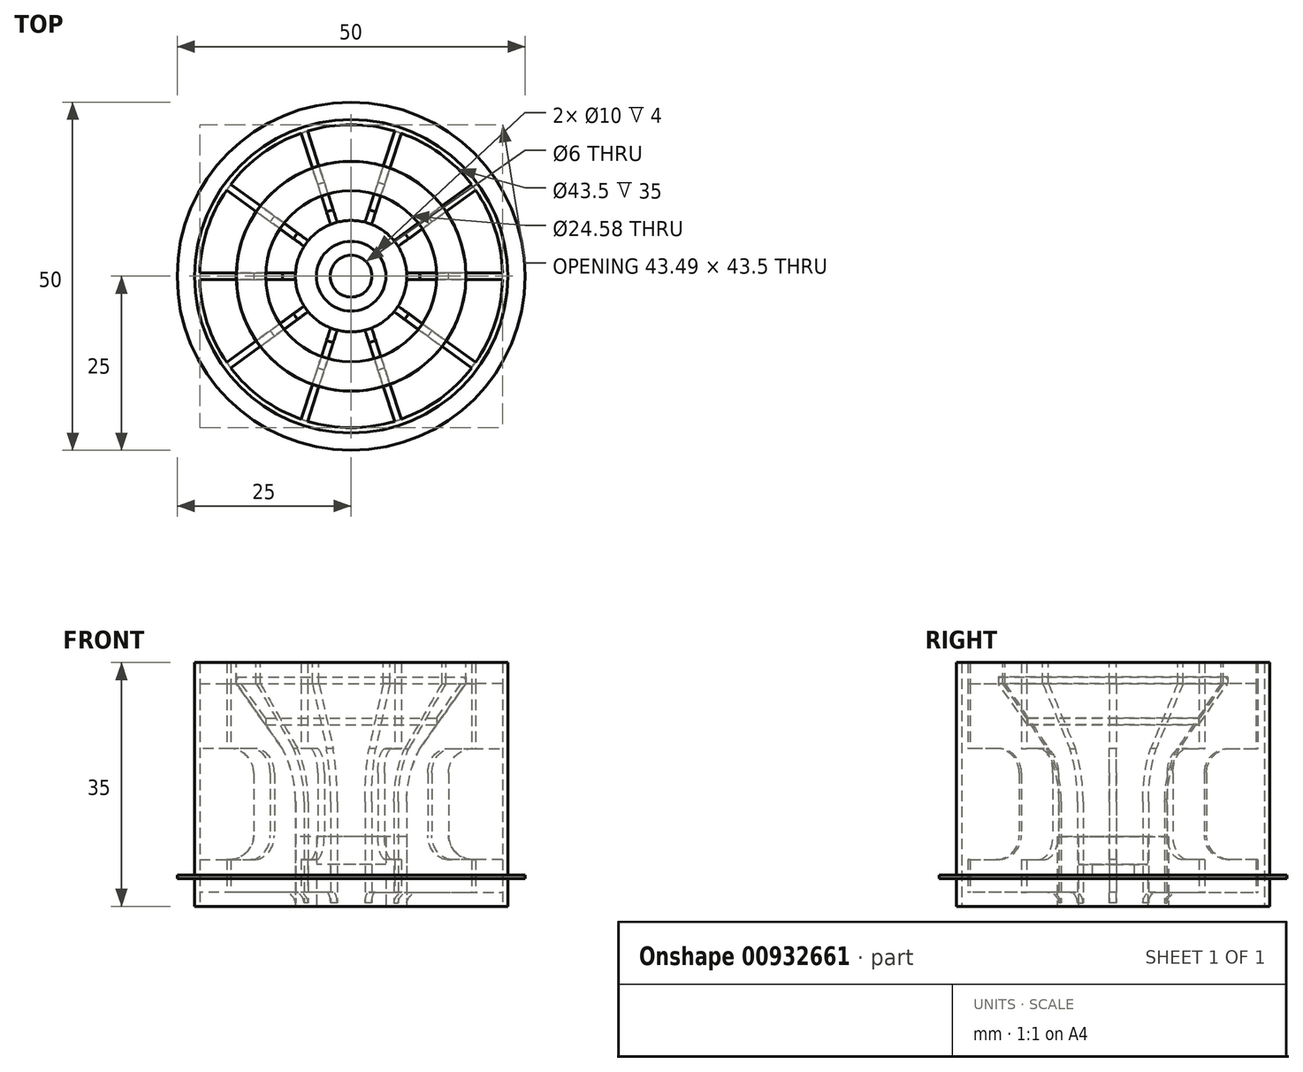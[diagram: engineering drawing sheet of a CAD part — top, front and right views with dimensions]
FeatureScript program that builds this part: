
annotation { "Feature Type Name" : "Feature", "Feature Type Description" : "" }
export const myFeature = defineFeature(function(context is Context, id is Id, definition is map)
    precondition{}
    {
        {
            var Q0;
            Q0=qCreatedBy(makeId("Top.planeOp"),FACE);
            var sketch = newSketch(context, id + "F0", { "sketchPlane" : qUnion([Q0])});
            skCircle(sketch, "E0", {"center": v(0, 0) * mm, "radius": 22.5 * mm});
            skCircle(sketch, "E1", {"center": v(0, 0) * mm, "radius": 21.75 * mm});
            skCircle(sketch, "E2", {"center": v(0, 0) * mm, "radius": 5 * mm});
            skCircle(sketch, "E3", {"center": v(0, 0) * mm, "radius": 8 * mm});
            skSolve(sketch);
        }
        {
            var Q0;
            Q0=makeQuery(id+"F0.imprint","IMPRINT",FACE,{"disambiguationData":[TD([[makeQuery(id+"F0.imprint","IMPRINT",EDGE,{"derivedFrom":sQuery(id+"F0.wireOp",EDGE,"E0")}),1.0]])]});
            extrude(context, id + "F1", {"entities" : qUnion([Q0]), "depth" : 35 * mm, "offsetDistance" : 25 * mm});
        }
        {
            var Q0;
            Q0=makeQuery(id+"F0.imprint","IMPRINT",FACE,{"disambiguationData":[TD([[makeQuery(id+"F0.imprint","IMPRINT",EDGE,{"derivedFrom":sQuery(id+"F0.wireOp",EDGE,"E2")}),-1.0]])]});
            extrude(context, id + "F2", {"entities" : qUnion([Q0]), "depth" : 4 * mm, "offsetDistance" : 25 * mm});
        }
        {
            var Q0;
            Q0=makeQuery(id+"F2.opExtrude","CAP_FACE",FACE,{"disambiguationData":[OSD([sQuery(id+"F0.wireOp",EDGE,"E2"),sQuery(id+"F0.wireOp",EDGE,"E3")])],"isStart":false});
            var sketch = newSketch(context, id + "F3", { "sketchPlane" : qUnion([Q0])});
            skCircle(sketch, "E4", {"center": v(0, 0) * mm, "radius": 3 * mm});
            skCircle(sketch, "E5", {"center": v(0, 0) * mm, "radius": 8 * mm});
            skSolve(sketch);
        }
        {
            var Q0;
            Q0=makeQuery(id+"F3.imprint","IMPRINT",FACE,{"disambiguationData":[TD([[makeQuery(id+"F3.imprint","IMPRINT",EDGE,{"derivedFrom":sQuery(id+"F3.wireOp",EDGE,"E5")}),1.0]])]});
            var Q1;
            Q1=makeQuery(id+"F3.imprint","IMPRINT",FACE,{"disambiguationData":[TD([[makeQuery(id+"F3.imprint","IMPRINT",EDGE,{"derivedFrom":sQuery(id+"F3.wireOp",EDGE,"E4")}),-1.0]])]});
            extrude(context, id + "F4", {"entities" : qUnion([Q0, Q1]), "operationType" : NewBodyOperationType.ADD, "depth" : 2 * mm, "offsetDistance" : 25 * mm});
        }
        {
            var Q0;
            Q0=makeQuery(id+"F4.opExtrude","CAP_FACE",FACE,{"disambiguationData":[OSD([sQuery(id+"F3.wireOp",EDGE,"E4"),sQuery(id+"F3.wireOp",EDGE,"E5")])],"isStart":false});
            var sketch = newSketch(context, id + "F5", { "sketchPlane" : qUnion([Q0])});
            skCircle(sketch, "E6", {"center": v(0, 0) * mm, "radius": 8 * mm});
            skCircle(sketch, "E7", {"center": v(0, 0) * mm, "radius": 5 * mm});
            skSolve(sketch);
        }
        {
            var Q0;
            Q0=makeQuery(id+"F5.imprint","IMPRINT",FACE,{"disambiguationData":[TD([[makeQuery(id+"F5.imprint","IMPRINT",EDGE,{"derivedFrom":sQuery(id+"F5.wireOp",EDGE,"E6")}),1.0]])]});
            extrude(context, id + "F6", {"entities" : qUnion([Q0]), "operationType" : NewBodyOperationType.ADD, "depth" : 4 * mm, "offsetDistance" : 25 * mm});
        }
        {
            var Q0;
            Q0=makeQuery(id+"F1.opExtrude","CAP_FACE",FACE,{"disambiguationData":[OSD([sQuery(id+"F0.wireOp",EDGE,"E0"),sQuery(id+"F0.wireOp",EDGE,"E1")])],"isStart":false});
            var sketch = newSketch(context, id + "F7", { "sketchPlane" : qUnion([Q0])});
            skCircle(sketch, "E8", {"center": v(0, 0) * mm, "radius": 16.5 * mm});
            skCircle(sketch, "E9", {"center": v(0, 0) * mm, "radius": 22.5 * mm});
            skSolve(sketch);
        }
        {
            var Q0;
            Q0=makeQuery(id+"F7.imprint","IMPRINT",FACE,{"disambiguationData":[TD([[makeQuery(id+"F7.imprint","IMPRINT",EDGE,{"derivedFrom":sQuery(id+"F7.wireOp",EDGE,"E8")}),-1.0]])]});
            extrude(context, id + "F8", {"entities" : qUnion([Q0]), "operationType" : NewBodyOperationType.ADD, "oppositeDirection" : true, "depth" : 3 * mm, "offsetDistance" : 25 * mm});
        }
        {
            var Q0;
            Q0=qCreatedBy(makeId("Front.planeOp"),FACE);
            var sketch = newSketch(context, id + "F9", { "sketchPlane" : qUnion([Q0])});
            skLineSegment(sketch, "E10.left", {"start": v(0, 0) * mm, "end": v(0, 6.73) * mm});
            skLineSegment(sketch, "E10.right", {"start": v(-8, 2) * mm, "end": v(-8, 15) * mm});
            skLineSegment(sketch, "E11.top", {"start": v(-16.5, 32) * mm, "end": v(-21, 32) * mm});
            skLineSegment(sketch, "E11.left", {"start": v(0, 0) * mm, "end": v(0, 32) * mm});
            skLineSegment(sketch, "E12", {"start": v(-21, 32) * mm, "end": v(-16.5, 32) * mm});
            skLineSegment(sketch, "E13", {"start": v(-16.5, 32) * mm, "end": v(-9.88, 22.65) * mm});
            skArc(sketch, "E14", {"start": v(-8, 15) * mm, "mid": v(-8.48, 18.94) * mm, "end": v(-9.88, 22.65) * mm});
            skPoint(sketch, "E15.left.end.orphan", {"position": v(-8, 20) * mm});
            skLineSegment(sketch, "E16", {"start": v(-15.83, 32) * mm, "end": v(-12.3, 27) * mm});
            skLineSegment(sketch, "E17", {"start": v(-12.3, 27) * mm, "end": v(-12.3, 26.06) * mm});
            skLineSegment(sketch, "E18", {"start": v(-15.83, 32) * mm, "end": v(-16.5, 32.94) * mm});
            skLineSegment(sketch, "E19", {"start": v(-16.5, 32.94) * mm, "end": v(-16.5, 32) * mm});
            skLineSegment(sketch, "E20.top", {"start": v(-9.71, 2) * mm, "end": v(-21, 2) * mm});
            skPoint(sketch, "E11.bottom.start.orphan", {"position": v(-8, 0) * mm});
            skArc(sketch, "E21", {"start": v(-8, 0) * mm, "mid": v(-8.43, 1.41) * mm, "end": v(-9.79, 2) * mm});
            skPoint(sketch, "E21.second.point", {"position": v(-11.5, 0) * mm});
            skPoint(sketch, "E21.third.point", {"position": v(-9.79, 2) * mm});
            skLineSegment(sketch, "E22.bottom", {"start": v(-21, 6.73) * mm, "end": v(-17.5, 6.73) * mm});
            skLineSegment(sketch, "E22.top", {"start": v(-21, 22.65) * mm, "end": v(-17.7, 22.65) * mm});
            skLineSegment(sketch, "E22.right", {"start": v(-14, 10.23) * mm, "end": v(-14, 19.73) * mm});
            skPoint(sketch, "E23.orphan", {"position": v(-14, 22.65) * mm});
            skLineSegment(sketch, "E24", {"start": v(-17.7, 22.65) * mm, "end": v(-17.5, 22.65) * mm});
            skLineSegment(sketch, "E25.right", {"start": v(-14, 19.73) * mm, "end": v(-14, 19.15) * mm});
            skArc(sketch, "E26", {"start": v(-14, 19.15) * mm, "mid": v(-15.03, 21.62) * mm, "end": v(-17.5, 22.65) * mm});
            skPoint(sketch, "E27.start.orphan", {"position": v(-17.5, 6.73) * mm});
            skArc(sketch, "E28", {"start": v(-17.5, 6.73) * mm, "mid": v(-15.03, 7.75) * mm, "end": v(-14, 10.23) * mm});
            skPoint(sketch, "E29.bottom.start.orphan", {"position": v(-14, 6.73) * mm});
            skLineSegment(sketch, "E30", {"start": v(-8, 2) * mm, "end": v(-8, 0) * mm});
            skLineSegment(sketch, "E31", {"start": v(0, 0) * mm, "end": v(-22.5, 0) * mm});
            skLineSegment(sketch, "E32", {"start": v(-22.5, 0) * mm, "end": v(-22.5, 4) * mm});
            skLineSegment(sketch, "E33.bottom", {"start": v(-22.5, 4) * mm, "end": v(-25, 4) * mm});
            skLineSegment(sketch, "E33.top", {"start": v(-22.5, 4.5) * mm, "end": v(-25, 4.5) * mm});
            skLineSegment(sketch, "E33.left", {"start": v(-22.5, 4) * mm, "end": v(-22.5, 4.5) * mm});
            skLineSegment(sketch, "E33.right", {"start": v(-25, 4) * mm, "end": v(-25, 4.5) * mm});
            skLineSegment(sketch, "E34", {"start": v(-21, 2) * mm, "end": v(-21.75, 2) * mm});
            skLineSegment(sketch, "E35.top", {"start": v(-21, 6.73) * mm, "end": v(-21.75, 6.73) * mm});
            skLineSegment(sketch, "E35.right", {"start": v(-21.75, 2) * mm, "end": v(-21.75, 6.73) * mm});
            skLineSegment(sketch, "E36.bottom", {"start": v(-21, 22.65) * mm, "end": v(-21.75, 22.65) * mm});
            skLineSegment(sketch, "E36.top", {"start": v(-21, 32) * mm, "end": v(-21.75, 32) * mm});
            skLineSegment(sketch, "E36.right", {"start": v(-21.75, 22.65) * mm, "end": v(-21.75, 32) * mm});
            skSolve(sketch);
        }
        {
            var Q0;
            Q0=makeQuery(id+"F9.imprint","IMPRINT",FACE,{"disambiguationData":[TD([[makeQuery(id+"F9.imprint","IMPRINT",EDGE,{"derivedFrom":sQuery(id+"F9.wireOp",EDGE,"E10.right")}),1.0]])]});
            var Q1;
            Q1=sQuery(id+"F9.wireOp",EDGE,"E11.left");
            revolve(context, id + "F10", {"surfaceOperationType" : NewSurfaceOperationType.NEW, "entities" : qUnion([Q0]), "axis" : qUnion([Q1]), "revolveType" : RevolveType.FULL});
        }
        {
            var Q0;
            Q0=makeQuery(id+"F2.opExtrude","CAP_FACE",FACE,{"disambiguationData":[OSD([sQuery(id+"F0.wireOp",EDGE,"E2"),sQuery(id+"F0.wireOp",EDGE,"E3")])],"isStart":true});
            var sketch = newSketch(context, id + "F11", { "sketchPlane" : qUnion([Q0])});
            skCircle(sketch, "E37", {"center": v(0, 0) * mm, "radius": 8 * mm});
            skLineSegment(sketch, "E38", {"start": v(0, 0) * mm, "end": v(-21, 0) * mm});
            skLineSegment(sketch, "E39.bottom", {"start": v(-7.98, -0.5) * mm, "end": v(-21, -0.5) * mm});
            skLineSegment(sketch, "E39.top", {"start": v(-7.98, 0.5) * mm, "end": v(-21, 0.5) * mm});
            skPoint(sketch, "E39.middle", {"position": v(-10.5, 0) * mm});
            skLineSegment(sketch, "E40.1.0", {"start": v(-6.75, -4.29) * mm, "end": v(-17.28, -11.94) * mm});
            skPoint(sketch, "E40.1.1", {"position": v(-8.5, -6.17) * mm});
            skLineSegment(sketch, "E40.1.2", {"start": v(-6.17, -5.1) * mm, "end": v(-16.7, -12.74) * mm});
            skLineSegment(sketch, "E40.2.0", {"start": v(-2.94, -7.44) * mm, "end": v(-6.96, -19.81) * mm});
            skPoint(sketch, "E40.2.1", {"position": v(-3.24, -9.99) * mm});
            skLineSegment(sketch, "E40.2.2", {"start": v(-2, -7.75) * mm, "end": v(-6.01, -20.12) * mm});
            skLineSegment(sketch, "E40.3.0", {"start": v(2, -7.75) * mm, "end": v(6.01, -20.12) * mm});
            skPoint(sketch, "E40.3.1", {"position": v(3.24, -9.99) * mm});
            skLineSegment(sketch, "E40.3.2", {"start": v(2.94, -7.44) * mm, "end": v(6.96, -19.81) * mm});
            skLineSegment(sketch, "E40.4.0", {"start": v(6.17, -5.1) * mm, "end": v(16.7, -12.74) * mm});
            skPoint(sketch, "E40.4.1", {"position": v(8.5, -6.17) * mm});
            skLineSegment(sketch, "E40.4.2", {"start": v(6.75, -4.29) * mm, "end": v(17.28, -11.94) * mm});
            skLineSegment(sketch, "E40.5.0", {"start": v(7.98, -0.5) * mm, "end": v(21, -0.5) * mm});
            skPoint(sketch, "E40.5.1", {"position": v(10.5, 0) * mm});
            skLineSegment(sketch, "E40.5.2", {"start": v(7.98, 0.5) * mm, "end": v(21, 0.5) * mm});
            skLineSegment(sketch, "E40.6.0", {"start": v(6.75, 4.29) * mm, "end": v(17.28, 11.94) * mm});
            skPoint(sketch, "E40.6.1", {"position": v(8.5, 6.17) * mm});
            skLineSegment(sketch, "E40.6.2", {"start": v(6.17, 5.1) * mm, "end": v(16.7, 12.74) * mm});
            skLineSegment(sketch, "E40.7.0", {"start": v(2.94, 7.44) * mm, "end": v(6.96, 19.81) * mm});
            skPoint(sketch, "E40.7.1", {"position": v(3.24, 9.99) * mm});
            skLineSegment(sketch, "E40.7.2", {"start": v(2, 7.75) * mm, "end": v(6.01, 20.12) * mm});
            skLineSegment(sketch, "E40.8.0", {"start": v(-2, 7.75) * mm, "end": v(-6.01, 20.12) * mm});
            skPoint(sketch, "E40.8.1", {"position": v(-3.24, 9.99) * mm});
            skLineSegment(sketch, "E40.8.2", {"start": v(-2.94, 7.44) * mm, "end": v(-6.96, 19.81) * mm});
            skLineSegment(sketch, "E40.9.0", {"start": v(-6.17, 5.1) * mm, "end": v(-16.7, 12.74) * mm});
            skPoint(sketch, "E40.9.1", {"position": v(-8.5, 6.17) * mm});
            skLineSegment(sketch, "E40.9.2", {"start": v(-6.75, 4.29) * mm, "end": v(-17.28, 11.94) * mm});
            skCircle(sketch, "E41", {"center": v(0, 0) * mm, "radius": 21.75 * mm});
            skLineSegment(sketch, "E42", {"start": v(-21, -0.5) * mm, "end": v(-21.74, -0.5) * mm});
            skLineSegment(sketch, "E43", {"start": v(-21, 0.5) * mm, "end": v(-21.74, 0.5) * mm});
            skLineSegment(sketch, "E44.1.0", {"start": v(-17.28, -11.94) * mm, "end": v(-17.89, -12.38) * mm});
            skLineSegment(sketch, "E44.1.1", {"start": v(-16.7, -12.74) * mm, "end": v(-17.3, -13.19) * mm});
            skLineSegment(sketch, "E44.2.0", {"start": v(-6.96, -19.81) * mm, "end": v(-7.2, -20.53) * mm});
            skLineSegment(sketch, "E44.2.1", {"start": v(-6.01, -20.12) * mm, "end": v(-6.24, -20.83) * mm});
            skLineSegment(sketch, "E44.3.0", {"start": v(6.01, -20.12) * mm, "end": v(6.24, -20.83) * mm});
            skLineSegment(sketch, "E44.3.1", {"start": v(6.96, -19.81) * mm, "end": v(7.2, -20.53) * mm});
            skLineSegment(sketch, "E44.4.0", {"start": v(16.7, -12.74) * mm, "end": v(17.3, -13.19) * mm});
            skLineSegment(sketch, "E44.4.1", {"start": v(17.28, -11.94) * mm, "end": v(17.89, -12.38) * mm});
            skLineSegment(sketch, "E44.5.0", {"start": v(21, -0.5) * mm, "end": v(21.74, -0.5) * mm});
            skLineSegment(sketch, "E44.5.1", {"start": v(21, 0.5) * mm, "end": v(21.74, 0.5) * mm});
            skLineSegment(sketch, "E44.6.0", {"start": v(17.28, 11.94) * mm, "end": v(17.89, 12.38) * mm});
            skLineSegment(sketch, "E44.6.1", {"start": v(16.7, 12.74) * mm, "end": v(17.3, 13.19) * mm});
            skLineSegment(sketch, "E44.7.0", {"start": v(6.96, 19.81) * mm, "end": v(7.2, 20.53) * mm});
            skLineSegment(sketch, "E44.7.1", {"start": v(6.01, 20.12) * mm, "end": v(6.24, 20.83) * mm});
            skLineSegment(sketch, "E44.8.0", {"start": v(-6.01, 20.12) * mm, "end": v(-6.24, 20.83) * mm});
            skLineSegment(sketch, "E44.8.1", {"start": v(-6.96, 19.81) * mm, "end": v(-7.2, 20.53) * mm});
            skLineSegment(sketch, "E44.9.0", {"start": v(-16.7, 12.74) * mm, "end": v(-17.3, 13.19) * mm});
            skLineSegment(sketch, "E44.9.1", {"start": v(-17.28, 11.94) * mm, "end": v(-17.89, 12.38) * mm});
            skSolve(sketch);
        }
        {
            var Q0;
            {var subQ0=sQuery(id+"F11.wireOp",EDGE,"E39.top");Q0=makeQuery(id+"F11.imprint","IMPRINT",FACE,{"disambiguationData":[TD([[makeQuery(id+"F11.imprint","IMPRINT",EDGE,{"derivedFrom":subQ0}),-1.0]])]});}
            var Q1;
            {var subQ0=sQuery(id+"F11.wireOp",EDGE,"E40.8.2");Q1=makeQuery(id+"F11.imprint","IMPRINT",FACE,{"disambiguationData":[TD([[makeQuery(id+"F11.imprint","IMPRINT",EDGE,{"derivedFrom":subQ0}),1.0]])]});}
            var Q2;
            {var subQ0=sQuery(id+"F11.wireOp",EDGE,"E40.7.2");Q2=makeQuery(id+"F11.imprint","IMPRINT",FACE,{"disambiguationData":[TD([[makeQuery(id+"F11.imprint","IMPRINT",EDGE,{"derivedFrom":subQ0}),1.0]])]});}
            var Q3;
            {var subQ0=sQuery(id+"F11.wireOp",EDGE,"E40.6.2");Q3=makeQuery(id+"F11.imprint","IMPRINT",FACE,{"disambiguationData":[TD([[makeQuery(id+"F11.imprint","IMPRINT",EDGE,{"derivedFrom":subQ0}),1.0]])]});}
            var Q4;
            {var subQ0=sQuery(id+"F11.wireOp",EDGE,"E40.5.2");Q4=makeQuery(id+"F11.imprint","IMPRINT",FACE,{"disambiguationData":[TD([[makeQuery(id+"F11.imprint","IMPRINT",EDGE,{"derivedFrom":subQ0}),1.0]])]});}
            var Q5;
            {var subQ0=sQuery(id+"F11.wireOp",EDGE,"E40.4.2");Q5=makeQuery(id+"F11.imprint","IMPRINT",FACE,{"disambiguationData":[TD([[makeQuery(id+"F11.imprint","IMPRINT",EDGE,{"derivedFrom":subQ0}),1.0]])]});}
            var Q6;
            {var subQ0=sQuery(id+"F11.wireOp",EDGE,"E40.3.2");Q6=makeQuery(id+"F11.imprint","IMPRINT",FACE,{"disambiguationData":[TD([[makeQuery(id+"F11.imprint","IMPRINT",EDGE,{"derivedFrom":subQ0}),1.0]])]});}
            var Q7;
            {var subQ0=sQuery(id+"F11.wireOp",EDGE,"E40.2.2");Q7=makeQuery(id+"F11.imprint","IMPRINT",FACE,{"disambiguationData":[TD([[makeQuery(id+"F11.imprint","IMPRINT",EDGE,{"derivedFrom":subQ0}),1.0]])]});}
            var Q8;
            {var subQ0=sQuery(id+"F11.wireOp",EDGE,"E40.1.2");Q8=makeQuery(id+"F11.imprint","IMPRINT",FACE,{"disambiguationData":[TD([[makeQuery(id+"F11.imprint","IMPRINT",EDGE,{"derivedFrom":subQ0}),1.0]])]});}
            var Q9;
            {var subQ0=sQuery(id+"F11.wireOp",EDGE,"E39.bottom");Q9=makeQuery(id+"F11.imprint","IMPRINT",FACE,{"disambiguationData":[TD([[makeQuery(id+"F11.imprint","IMPRINT",EDGE,{"derivedFrom":subQ0}),1.0]])]});}
            extrude(context, id + "F12", {"entities" : qUnion([Q0, Q1, Q2, Q3, Q4, Q5, Q6, Q7, Q8, Q9]), "operationType" : NewBodyOperationType.REMOVE, "oppositeDirection" : true, "depth" : 35 * mm, "offsetDistance" : 25 * mm});
        }
        {
            var Q0;
            Q0=makeQuery(id+"F9.imprint","IMPRINT",FACE,{"disambiguationData":[TD([[makeQuery(id+"F9.imprint","IMPRINT",EDGE,{"derivedFrom":sQuery(id+"F9.wireOp",EDGE,"E16")}),-1.0]])]});
            var Q1;
            Q1=sQuery(id+"F9.wireOp",EDGE,"E11.left");
            revolve(context, id + "F13", {"surfaceOperationType" : NewSurfaceOperationType.NEW, "entities" : qUnion([Q0]), "axis" : qUnion([Q1]), "revolveType" : RevolveType.FULL});
        }
        {
            var Q0;
            Q0=makeQuery(id+"F9.imprint","IMPRINT",FACE,{"disambiguationData":[TD([[makeQuery(id+"F9.imprint","IMPRINT",EDGE,{"derivedFrom":sQuery(id+"F9.wireOp",EDGE,"E33.bottom")}),-1.0]])]});
            var Q1;
            Q1=sQuery(id+"F9.wireOp",EDGE,"E11.left");
            revolve(context, id + "F14", {"operationType" : NewBodyOperationType.ADD, "surfaceOperationType" : NewSurfaceOperationType.NEW, "entities" : qUnion([Q0]), "axis" : qUnion([Q1]), "revolveType" : RevolveType.FULL});
        }
    });
